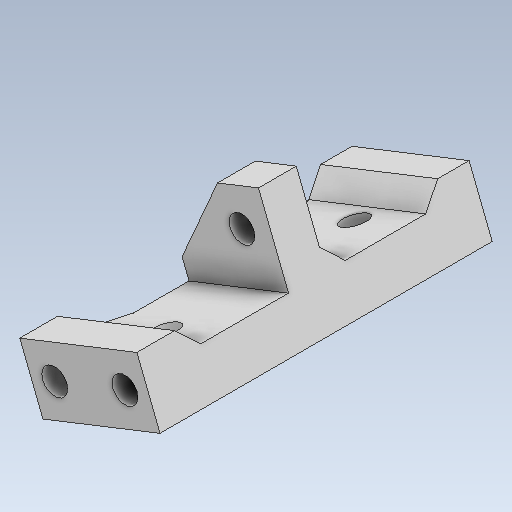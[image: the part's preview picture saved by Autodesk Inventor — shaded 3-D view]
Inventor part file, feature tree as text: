
AUTODESK INVENTOR PART (.ipt)
format: ipt  version: 2020 (Build 240168000, 168)  size: 307,200 bytes
history: native  units: mm
features: projected_geometry x11, extrude x10, sketch x10, chamfer x5, other x3, plane x2, thicken_offset x1, reference x1
ambient origin geometry x8: Origin, YZ Plane, XZ Plane, XY Plane, X Axis, Y Axis, Z Axis, Center Point
bodies: Solid1 (feature_tree)
feature tree (43):
  extrude  "Extrusion1"  Depth=20.0mm
  sketch  "Sketch2"  dims[d2=10.0mm d3=20.0mm d4=5.0mm d5=0.0mm]
  plane  "Work Plane1"
  extrude  "Extrusion2"  Depth=20.0mm
  chamfer  "Chamfer1"  Distance=5.0mm
  extrude  "Extrusion3"  Depth=7.0mm TaperAngle=0.0deg
  extrude  "Extrusion6"  Depth=6.0mm
  extrude  "Extrusion7"  Depth=6.0mm
  thicken_offset  "Thicken1"
  chamfer  "Chamfer2"  Distance=6.0mm
  sketch  "Sketch9"  dims[d15=4.1mm d16=6.0mm d17=0.0mm]
  plane  "Work Plane2"
  extrude  "Extrusion8"  Depth=15.0mm
  extrude  "Extrusion9"  Depth=6.0mm
  chamfer  "Chamfer3"  Distance=6.0mm
  extrude  "Extrusion11"  Depth=2.0mm
  chamfer  "Chamfer4"  Distance=2.0mm
  chamfer  "Chamfer5"  Distance=3.0mm Angle=45.0deg
  extrude  "Extrusion12"  Depth=6.0mm TaperAngle=0.0deg
  extrude  "Extrusion13"  Depth=20.0mm
  sketch  "Sketch1"  dims[d0=42.0mm d1=20.0mm]
  reference  "Reference1"
  projected_geometry  "Projected Loop1"
  sketch  "Sketch3"  dims[d6=7.0mm d7=5.0mm d8=0.0mm]
  projected_geometry  "Projected Loop2"
  sketch  "Sketch6"  dims[d9=3.0mm d10=2.0mm d11=45.0deg d12=6.0mm]
  projected_geometry  "Projected Loop5"
  sketch  "Sketch7"  dims[d13=6.0mm d14=4.1mm]
  projected_geometry  "Projected Loop6"
  projected_geometry  "Projected Loop7"
  sketch  "Sketch10"  dims[d30=15.0mm d31=5.0mm]
  projected_geometry  "Projected Loop8"
  sketch  "Sketch12"  dims[d32=6.0mm d33=0.0mm d34=7.5mm]
  projected_geometry  "Projected Loop10"
  projected_geometry  "Projected Loop11"
  projected_geometry  "Projected Loop12"
  sketch  "Sketch13"  dims[d35=5.0mm]
  projected_geometry  "Projected Loop13"
  sketch  "Sketch14"  dims[d36=4.1mm d37=6.0mm d38=0.0mm d40=2.0mm d41=2.0mm d42=3.0mm d43=2.0mm d44=45.0deg d45=6.0mm d46=0.0mm d47=20.0mm d48=10.0mm d49=6.0mm d50=0.0mm d51=3.0mm d52=2.0mm d53=45.0deg d61=20.0mm d62=0.0mm d63=3.0mm d64=2.0mm d65=60.0deg d66=3.0mm d67=2.0mm d68=60.0deg d69=8.0mm d70=0.0mm d71=4.0mm d72=15.0mm d73=15.0mm d74=4.0mm d75=4.0mm d76=8.0mm d77=0.0mm]
  projected_geometry  "Projected Loop14"
  parser-record x1  (decoder bookkeeping rows leaked as tree rows — omitted from the tree; the rows remain in map.json)
  other  "reducer_1.iam"
  other  "motor_holder_1:1"
note: 1 file-system path scrubbed to <path> (originals preserved in map.json)
